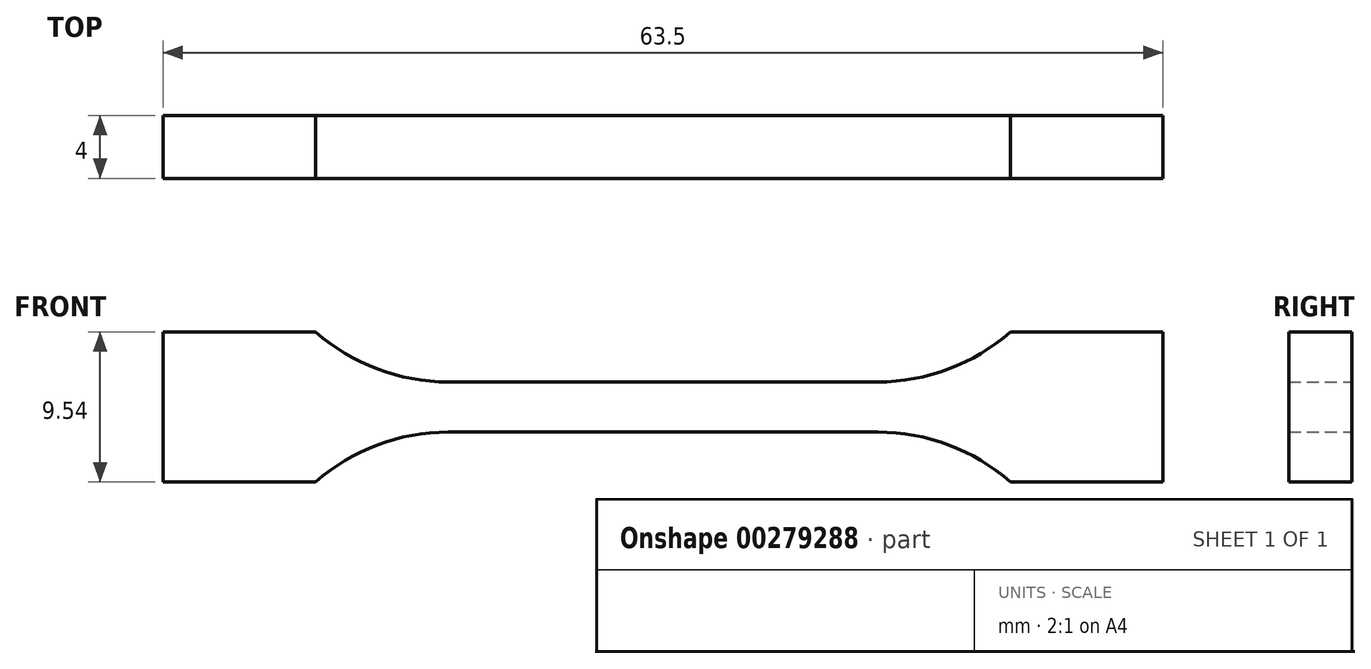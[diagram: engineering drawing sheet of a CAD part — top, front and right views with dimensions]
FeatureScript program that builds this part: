
annotation { "Feature Type Name" : "Feature", "Feature Type Description" : "" }
export const myFeature = defineFeature(function(context is Context, id is Id, definition is map)
    precondition{}
    {
        {
            var Q0;
            Q0=qCreatedBy(makeId("Front.planeOp"),FACE);
            var sketch = newSketch(context, id + "F0", { "sketchPlane" : qUnion([Q0])});
            skLineSegment(sketch, "E0", {"start": v(0, 1.59) * mm, "end": v(13.65, 1.59) * mm});
            skArc(sketch, "E1", {"start": v(13.65, 1.6) * mm, "mid": v(18.14, 2.41) * mm, "end": v(22.05, 4.77) * mm});
            skLineSegment(sketch, "E2", {"start": v(22.05, 4.76) * mm, "end": v(31.75, 4.77) * mm});
            skLineSegment(sketch, "E3.MirrorCS", {"start": v(0, -1.6) * mm, "end": v(13.65, -1.6) * mm});
            skLineSegment(sketch, "E4.MirrorCS", {"start": v(22.05, -4.77) * mm, "end": v(31.75, -4.76) * mm});
            skArc(sketch, "E5.MirrorCS", {"start": v(13.65, -1.6) * mm, "mid": v(18.14, -2.41) * mm, "end": v(22.05, -4.77) * mm});
            skArc(sketch, "E6.MirrorCS", {"start": v(-13.65, -1.6) * mm, "mid": v(-18.14, -2.41) * mm, "end": v(-22.05, -4.77) * mm});
            skLineSegment(sketch, "E7.MirrorCS", {"start": v(0, 1.6) * mm, "end": v(-13.65, 1.59) * mm});
            skArc(sketch, "E8.MirrorCS", {"start": v(-13.65, 1.6) * mm, "mid": v(-18.14, 2.41) * mm, "end": v(-22.05, 4.77) * mm});
            skLineSegment(sketch, "E9.MirrorCS", {"start": v(0, -1.59) * mm, "end": v(-13.65, -1.6) * mm});
            skLineSegment(sketch, "E10.MirrorCS", {"start": v(-22.05, 4.76) * mm, "end": v(-31.75, 4.76) * mm});
            skLineSegment(sketch, "E11.MirrorCS", {"start": v(-22.05, -4.77) * mm, "end": v(-31.75, -4.77) * mm});
            skLineSegment(sketch, "E12", {"start": v(-31.75, 4.77) * mm, "end": v(-31.75, -4.77) * mm});
            skLineSegment(sketch, "E13", {"start": v(31.75, -4.77) * mm, "end": v(31.75, 4.77) * mm});
            skSolve(sketch);
        }
        {
            var Q0;
            Q0 = qSketchRegion(id + "F0", true);
            extrude(context, id + "F1", {"entities" : qUnion([Q0]), "endBound" : BoundingType.SYMMETRIC, "depth" : 4 * mm});
        }
    });
